# Revit family: Точечный двустворчатый люк M8CITY_2017
name_source: partatom
category: Окна
revit_build: Autodesk Revit 2017 (Build: 20170118_1100(x64)
units: mm (PartAtom-declared; Revit-internal decimal feet)

## family parameters
Всегда вертикально = Нет
Общий = Нет
Основа = Крыша
При загрузке вырезать с полостями = Нет
Точка расчета площади = Нет

## types (1)
- Точечный двустворчатый люк M8CITY
    ADSK_Завод-изготовитель = ООО ''Завод М8 Сити''
    ADSK_Код изделия = ТУ BY 191302027.002-2013
    ADSK_Количество = 1
    ADSK_Обозначение = M8CITY
    ADSK_Размер_Высота = 400 мм
    ADSK_Размер_Длина = 3000 мм
    ADSK_Размер_Ширина = 1500 мм
    Table 1 = Описание
    Table 2 = Расчет
    Table 3 = Маркировка
    URL = www.m8city.by
    Высота = 473 мм
    Высота основания = 400 мм
    Длина = 3000 мм
    Длина проёма = 3000 мм
    Длина проёма ввод = 3000 мм
    Крышка плоская = 3
    Крышка формованная = 0
    ММ3.3 = Купол зенитного фонаря Ф st : МП молочный 3+3 мм
    ММ3.4 = Купол зенитного фонаря Ф st : МП молочный 3+4 мм
    МП3.3 = Купол зенитного фонаря Ф st : МП прозрачный 3+3 мм
    МП3.4 = Купол зенитного фонаря Ф st : МП прозрачный 3+4 мм
    ПКМ16 = Купол зенитного фонаря П pro : ПС молочный 16 мм
    ПКМ20 = Купол зенитного фонаря П pro : ПС молочный 20 мм
    ПКП16 = Купол зенитного фонаря П pro : ПС прозрачный 16 мм
    ПКП20 = Купол зенитного фонаря П pro : ПС прозрачный 20 мм
    СП26 = Купол зенитного фонаря П pro : СП 26 мм
    Установка привода = 1400 мм
    Форма = 1
    Ширина = 1500 мм
    Ширина проёма = 1500 мм
    Ширина проёма ввод = 1400 мм
